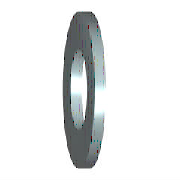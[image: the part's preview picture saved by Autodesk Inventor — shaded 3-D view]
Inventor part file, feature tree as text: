
AUTODESK INVENTOR PART (.ipt)
format: ipt  version: 2023.3 (Build 273359000, 359)  size: 107,008 bytes
history: native  units: mm (DEFAULTED — no unit token found)
features: extrude x1, other x1, plane x1, sketch x1
ambient origin geometry x7: Origin, YZ Plane, XY Plane, X Axis, Y Axis, Z Axis, Center Point
bodies: Solid1 (feature_tree)
feature tree (4):
  extrude  "Körper"  Depth=0.5mm
  other  "Work Axis1"
  plane  "Work Plane1"
  sketch  "Skizze"  dims[d0=2.9mm d1=6.0mm d2=0.5mm d3=0.0mm d4=0.0mm d5=0.0mm d6=0.0mm d7=0.0mm]
